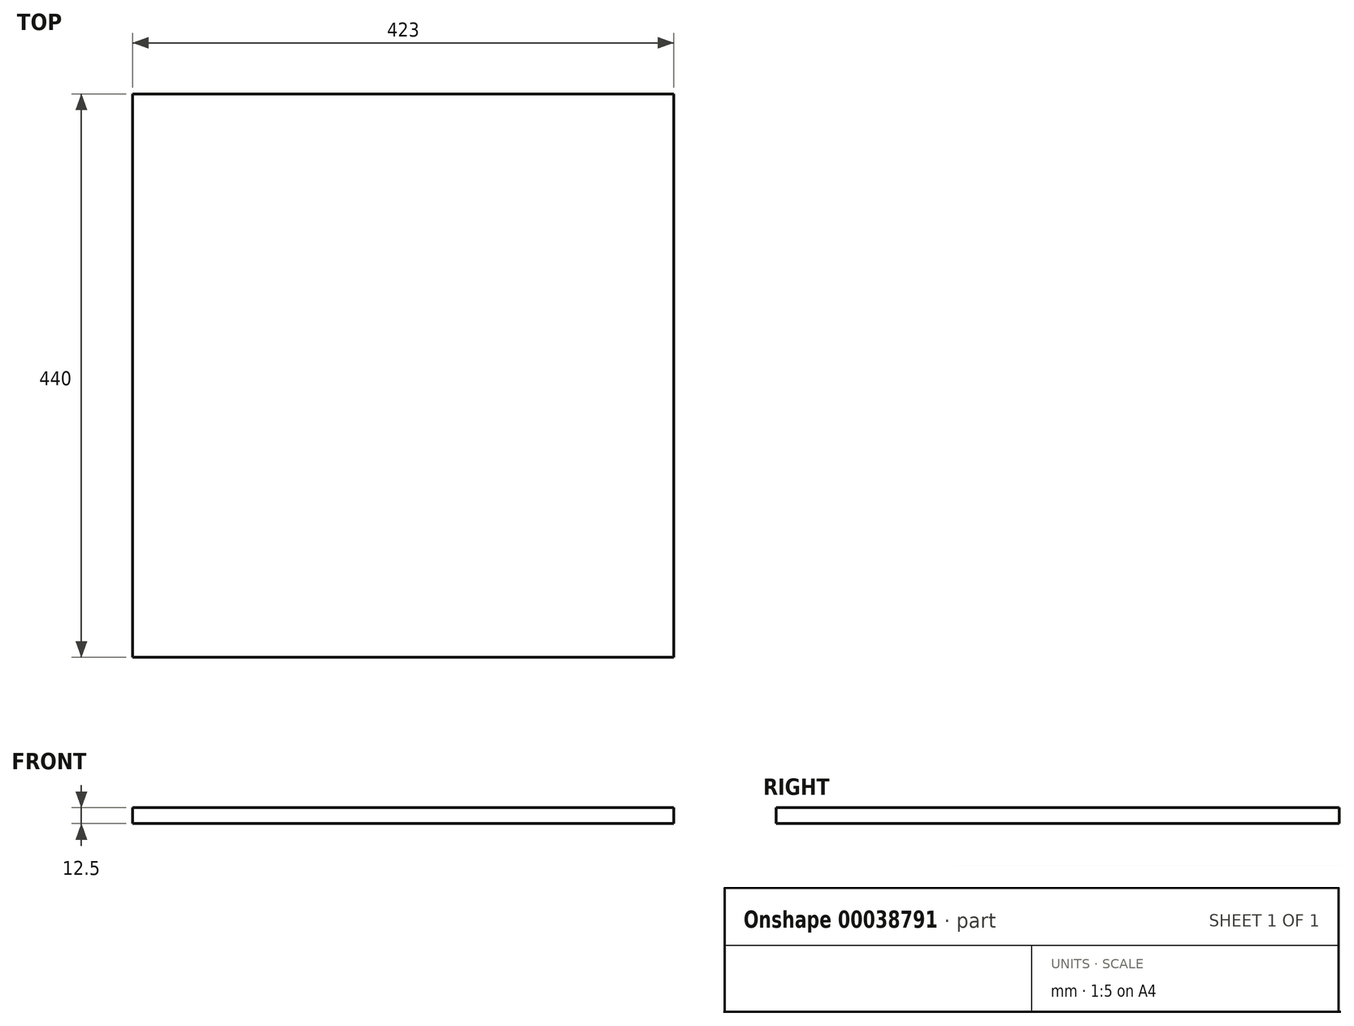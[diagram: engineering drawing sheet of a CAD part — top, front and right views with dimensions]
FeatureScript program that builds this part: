
annotation { "Feature Type Name" : "Feature", "Feature Type Description" : "" }
export const myFeature = defineFeature(function(context is Context, id is Id, definition is map)
    precondition{}
    {
        {
            var Q0;
            Q0=qCreatedBy(makeId("Top.planeOp"),FACE);
            var sketch = newSketch(context, id + "F0", { "sketchPlane" : qUnion([Q0])});
            skLineSegment(sketch, "E0.bottom", {"start": v(-70.96, 65.05) * mm, "end": v(352.04, 65.05) * mm});
            skLineSegment(sketch, "E0.top", {"start": v(-70.96, -374.95) * mm, "end": v(352.04, -374.95) * mm});
            skLineSegment(sketch, "E0.left", {"start": v(-70.96, 65.05) * mm, "end": v(-70.96, -374.95) * mm});
            skLineSegment(sketch, "E0.right", {"start": v(352.04, 65.05) * mm, "end": v(352.04, -374.95) * mm});
            skSolve(sketch);
        }
        {
            var Q0;
            Q0=qSketchRegion(id+"F0",true);
            extrude(context, id + "F1", {"entities" : qUnion([Q0]), "depth" : 12.5 * mm});
        }
    });
